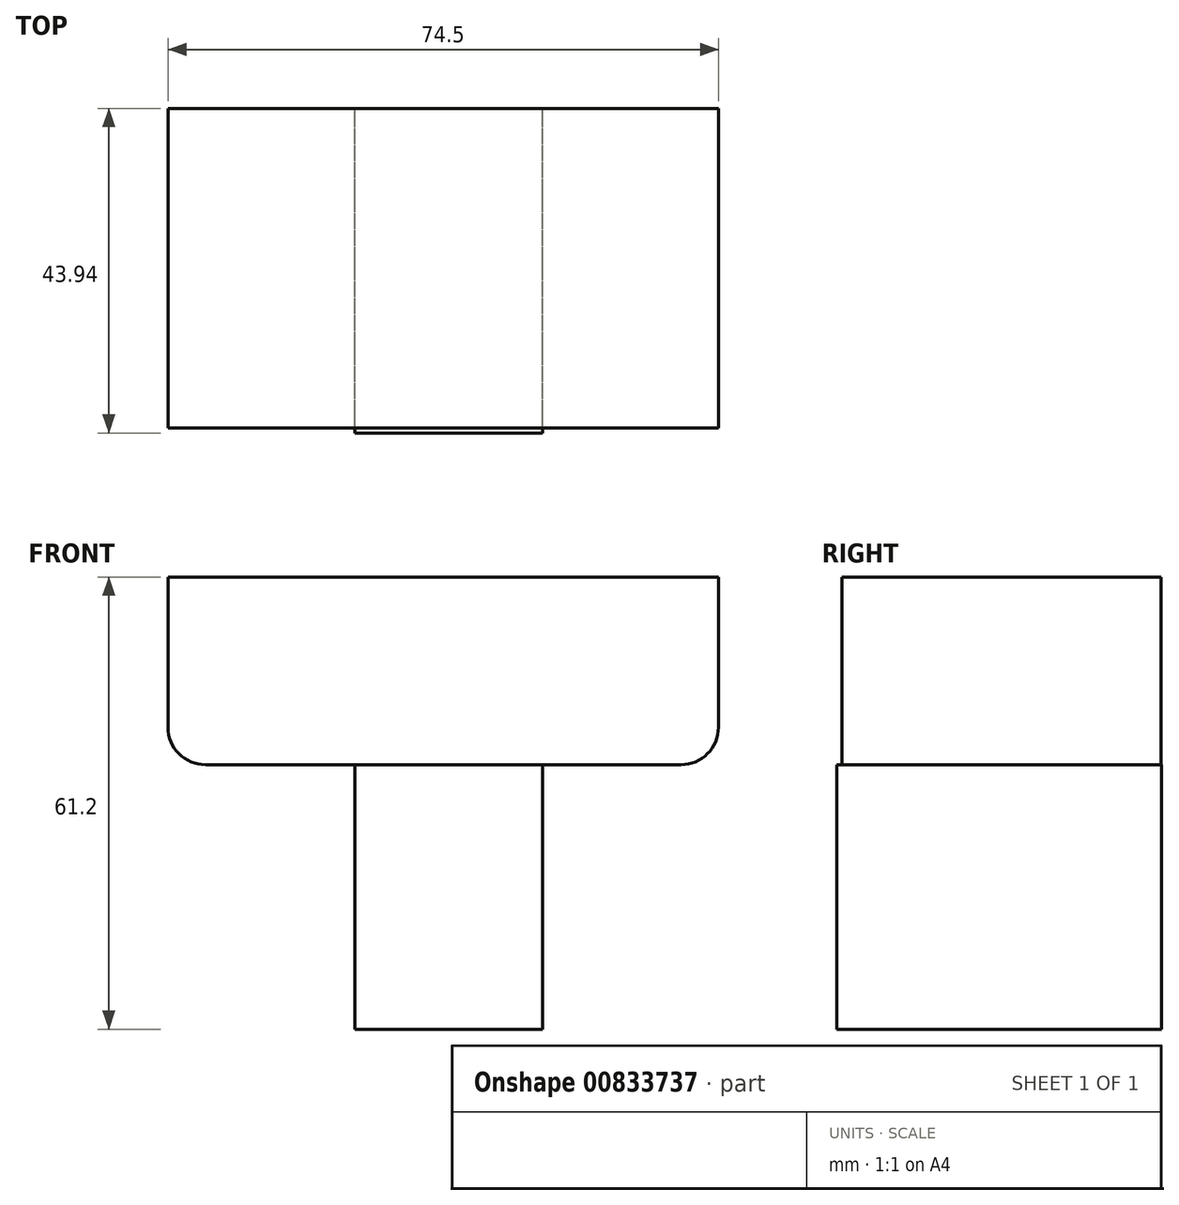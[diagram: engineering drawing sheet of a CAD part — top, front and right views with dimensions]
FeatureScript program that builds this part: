
annotation { "Feature Type Name" : "Feature", "Feature Type Description" : "" }
export const myFeature = defineFeature(function(context is Context, id is Id, definition is map)
    precondition{}
    {
        {
            var Q0;
            Q0=qCreatedBy(makeId("Top.planeOp"),FACE);
            var sketch = newSketch(context, id + "F0", { "sketchPlane" : qUnion([Q0])});
            skLineSegment(sketch, "E0.bottom", {"start": v(-25.3, 27.41) * mm, "end": v(49.2, 27.41) * mm});
            skLineSegment(sketch, "E0.top", {"start": v(-25.3, -15.8) * mm, "end": v(49.2, -15.8) * mm});
            skLineSegment(sketch, "E0.left", {"start": v(-25.3, 27.41) * mm, "end": v(-25.3, -15.8) * mm});
            skLineSegment(sketch, "E0.right", {"start": v(49.2, 27.41) * mm, "end": v(49.2, -15.8) * mm});
            skSolve(sketch);
        }
        {
            var Q0;
            Q0=qCreatedBy(makeId("Right.planeOp"),FACE);
            var sketch = newSketch(context, id + "F1", { "sketchPlane" : qUnion([Q0])});
            skLineSegment(sketch, "E1.bottom", {"start": v(-16.48, 0) * mm, "end": v(27.46, 0) * mm});
            skLineSegment(sketch, "E1.top", {"start": v(-16.48, -35.8) * mm, "end": v(27.46, -35.8) * mm});
            skLineSegment(sketch, "E1.left", {"start": v(-16.48, 0) * mm, "end": v(-16.48, -35.8) * mm});
            skLineSegment(sketch, "E1.right", {"start": v(27.46, 0) * mm, "end": v(27.46, -35.8) * mm});
            skPoint(sketch, "E2", {"position": v(17.4, -15.74) * mm});
            skSolve(sketch);
        }
        {
            var Q0;
            Q0=makeQuery(id+"F1.imprint","IMPRINT",FACE,{"disambiguationData":[TD([[makeQuery(id+"F1.imprint","IMPRINT",EDGE,{"derivedFrom":sQuery(id+"F1.wireOp",EDGE,"E1.bottom")}),-1.0]])]});
            extrude(context, id + "F2", {"entities" : qUnion([Q0]), "depth" : 25.4 * mm, "offsetDistance" : 25.4 * mm});
        }
        {
            var Q0;
            Q0=makeQuery(id+"F0.imprint","IMPRINT",FACE,{"disambiguationData":[TD([[makeQuery(id+"F0.imprint","IMPRINT",EDGE,{"derivedFrom":sQuery(id+"F0.wireOp",EDGE,"E0.bottom")}),-1.0]])]});
            extrude(context, id + "F3", {"entities" : qUnion([Q0]), "operationType" : NewBodyOperationType.ADD, "depth" : 25.4 * mm, "offsetDistance" : 25.4 * mm});
        }
        {
            var Q0;
            Q0=makeQuery(id+"F3.opExtrude","CAP_EDGE",EDGE,{"disambiguationData":[OSD([sQuery(id+"F0.wireOp",EDGE,"E0.right")])],"isStart":true});
            fillet(context, id + "F4", {"entities" : qUnion([Q0]), "radius" : 5.08 * mm, "tangentPropagation" : true, "allowEdgeOverflow" : false});
        }
        {
            var Q0;
            Q0=makeQuery(id+"F3.opExtrude","CAP_EDGE",EDGE,{"disambiguationData":[OSD([sQuery(id+"F0.wireOp",EDGE,"E0.left")])],"isStart":true});
            fillet(context, id + "F5", {"entities" : qUnion([Q0]), "radius" : 5.08 * mm, "tangentPropagation" : true, "allowEdgeOverflow" : false});
        }
    });
